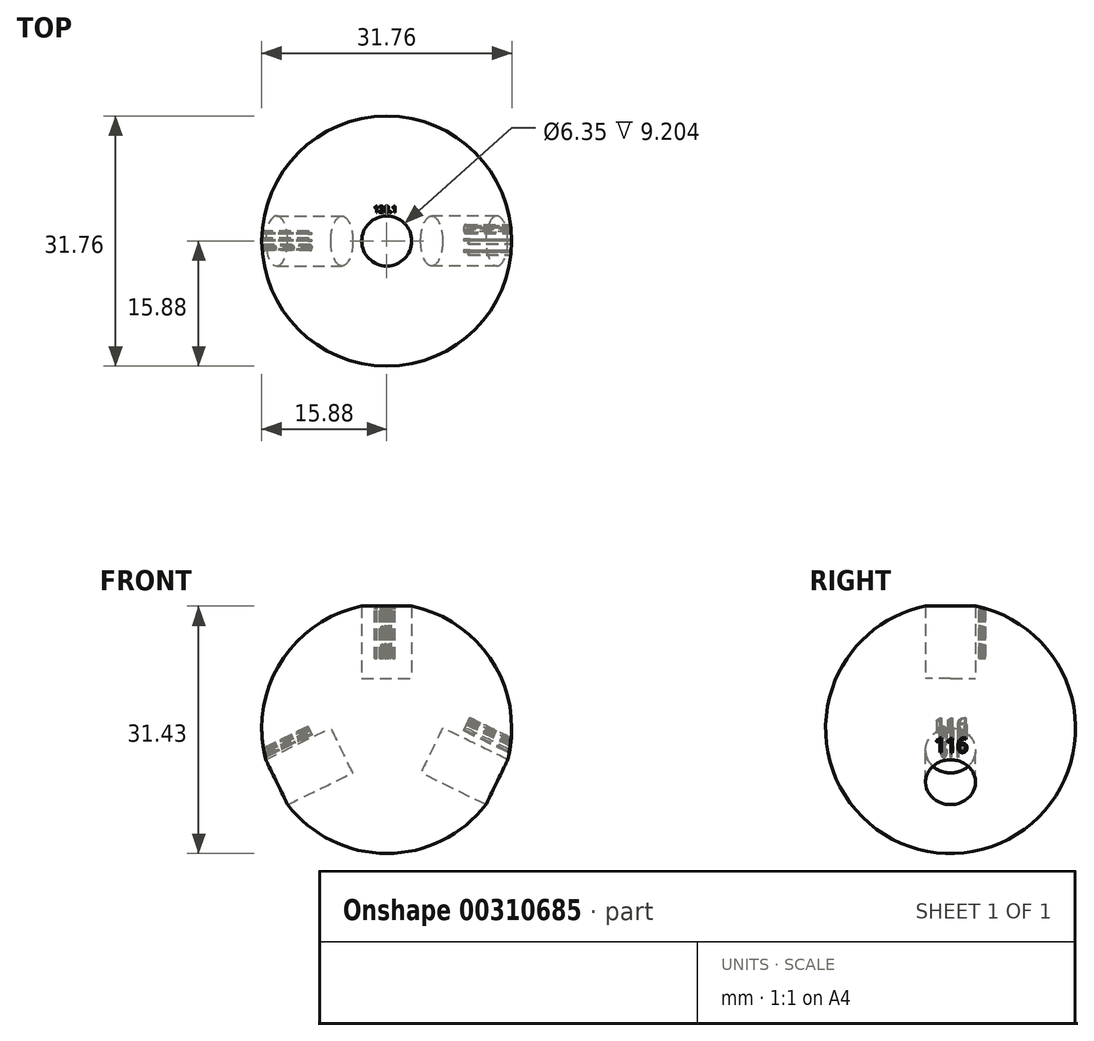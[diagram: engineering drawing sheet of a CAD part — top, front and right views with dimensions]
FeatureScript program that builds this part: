
annotation { "Feature Type Name" : "Feature", "Feature Type Description" : "" }
export const myFeature = defineFeature(function(context is Context, id is Id, definition is map)
    precondition{}
    {
        {
            var Q0;
            Q0=qCreatedBy(makeId("Front.planeOp"),FACE);
            var sketch = newSketch(context, id + "F0", { "sketchPlane" : qUnion([Q0])});
            skArc(sketch, "E0", {"start": v(-15.88, 0) * mm, "mid": v(0, -15.88) * mm, "end": v(15.88, 0) * mm});
            skLineSegment(sketch, "E1", {"start": v(-15.88, 0) * mm, "end": v(15.88, 0) * mm});
            skSolve(sketch);
        }
        {
            var Q0;
            Q0=qCreatedBy(makeId("Right.planeOp"),FACE);
            var sketch = newSketch(context, id + "F1", { "sketchPlane" : qUnion([Q0])});
            skCircle(sketch, "E2", {"center": v(0, 0) * mm, "radius": 15.88 * mm});
            skSolve(sketch);
        }
        {
            var Q0;
            Q0 = qSketchRegion(id + "F0", true);
            var Q1;
            Q1=sQuery(id+"F1.wireOp",EDGE,"E2");
            revolve(context, id + "F2", {"entities" : qUnion([Q0]), "axis" : qUnion([Q1]), "revolveType" : RevolveType.FULL});
        }
        {
            var Q0;
            Q0=qCreatedBy(makeId("Top.planeOp"),FACE);
            cPlane(context, id + "F3", {"entities" : qUnion([Q0]), "cplaneType" : CPlaneType.OFFSET, "offset" : 6.35 * mm, "width" : 152.4 * mm, "height" : 152.4 * mm});
        }
        {
            var Q0;
            Q0=qCreatedBy(id+"F3.planeOp",FACE);
            var sketch = newSketch(context, id + "F4", { "sketchPlane" : qUnion([Q0])});
            skCircle(sketch, "E3", {"center": v(0, 0) * mm, "radius": 3.18 * mm});
            skSolve(sketch);
        }
        {
            var Q0;
            Q0 = qSketchRegion(id + "F4", true);
            extrude(context, id + "F5", {"entities" : qUnion([Q0]), "depth" : 25.4 * mm});
        }
        {
            var Q0;
            Q0=makeQuery(id+"F5.opExtrude","CAP_FACE",FACE,{"disambiguationData":[OSD([sQuery(id+"F4.wireOp",EDGE,"E3")])],"isStart":false});
            cPlane(context, id + "F6", {"entities" : qUnion([Q0]), "cplaneType" : CPlaneType.OFFSET, "offset" : 12.7 * mm, "oppositeDirection" : true, "width" : 152.4 * mm, "height" : 152.4 * mm});
        }
        {
            var Q0;
            Q0=qCreatedBy(id+"F6.planeOp",FACE);
            var sketch = newSketch(context, id + "F7", { "sketchPlane" : qUnion([Q0])});
            skText(sketch, "E4", { "text": "128.1\n", "fontName": "OpenSans-Regular.ttf"});
            const initialGuessF7  = {"E4": [-0.00164, 0.00361, 1, 0, 0.00083]};
            skSetInitialGuess(sketch, initialGuessF7);
            skSolve(sketch);
        }
        {
            var Q0;
            Q0 = qSketchRegion(id + "F7", true);
            extrude(context, id + "F8", {"entities" : qUnion([Q0]), "operationType" : NewBodyOperationType.REMOVE, "oppositeDirection" : true, "depth" : 10.16 * mm});
        }
        {
            var Q0;
            Q0=qCreatedBy(makeId("Right.planeOp"),FACE);
            var sketch = newSketch(context, id + "F9", { "sketchPlane" : qUnion([Q0])});
            skLineSegment(sketch, "E5", {"start": v(66.37, 0) * mm, "end": v(-36.87, 0) * mm, "construction": true});
            skSolve(sketch);
        }
        {
            var Q0;
            Q0=makeQuery(id+"F5.opExtrude","SWEPT_BODY",BODY,{"disambiguationData":[OSD([sQuery(id+"F4.wireOp",EDGE,"E3")])]});
            var Q1;
            Q1=sQuery(id+"F9.wireOp",EDGE,"E5");
            transform(context, id + "F10", {"entities" : qUnion([Q0]), "transformType" : TransformType.ROTATION, "transformAxis" : qUnion([Q1]), "angle" : 116 * degree, "makeCopy" : true});
        }
        {
            var Q0;
            Q0=makeQuery(id+"F10.opPattern","COPY",FACE,{"derivedFrom":makeQuery(id+"F5.opExtrude","CAP_FACE",FACE,{"disambiguationData":[OSD([sQuery(id+"F4.wireOp",EDGE,"E3")])],"isStart":false}),"instanceName":"1"});
            cPlane(context, id + "F11", {"entities" : qUnion([Q0]), "cplaneType" : CPlaneType.OFFSET, "offset" : 12.7 * mm, "oppositeDirection" : true, "width" : 152.4 * mm, "height" : 152.4 * mm});
        }
        {
            var Q0;
            Q0=qCreatedBy(id+"F11.planeOp",FACE);
            var sketch = newSketch(context, id + "F12", { "sketchPlane" : qUnion([Q0])});
            skText(sketch, "E6", { "text": "116", "fontName": "OpenSans-Regular.ttf"});
            const initialGuessF12  = {"E6": [-0.00144, 0.00347, 1, 0, 0.00115]};
            skSetInitialGuess(sketch, initialGuessF12);
            skSolve(sketch);
        }
        {
            var Q0;
            Q0 = qSketchRegion(id + "F12", true);
            extrude(context, id + "F13", {"entities" : qUnion([Q0]), "operationType" : NewBodyOperationType.REMOVE, "oppositeDirection" : true, "depth" : 10.16 * mm});
        }
        {
            var Q0;
            Q0=qCreatedBy(makeId("Right.planeOp"),FACE);
            var sketch = newSketch(context, id + "F14", { "sketchPlane" : qUnion([Q0])});
            skLineSegment(sketch, "E7", {"start": v(59, 0) * mm, "end": v(-23.6, 0) * mm, "construction": true});
            skSolve(sketch);
        }
        {
            var Q0;
            Q0=makeQuery(id+"F5.opExtrude","SWEPT_BODY",BODY,{"disambiguationData":[OSD([sQuery(id+"F4.wireOp",EDGE,"E3")])]});
            var Q1;
            Q1=sQuery(id+"F14.wireOp",EDGE,"E7");
            transform(context, id + "F15", {"entities" : qUnion([Q0]), "transformType" : TransformType.ROTATION, "transformAxis" : qUnion([Q1]), "angle" : 116 * degree, "oppositeDirection" : true, "makeCopy" : true});
        }
        {
            var Q0;
            Q0=makeQuery(id+"F15.opPattern","COPY",FACE,{"derivedFrom":makeQuery(id+"F5.opExtrude","CAP_FACE",FACE,{"disambiguationData":[OSD([sQuery(id+"F4.wireOp",EDGE,"E3")])],"isStart":false}),"instanceName":"1"});
            cPlane(context, id + "F16", {"entities" : qUnion([Q0]), "cplaneType" : CPlaneType.OFFSET, "offset" : 12.7 * mm, "oppositeDirection" : true, "width" : 152.4 * mm, "height" : 152.4 * mm});
        }
        {
            var Q0;
            Q0=qCreatedBy(id+"F16.planeOp",FACE);
            var sketch = newSketch(context, id + "F17", { "sketchPlane" : qUnion([Q0])});
            skText(sketch, "E8", { "text": "116", "fontName": "OpenSans-Regular.ttf"});
            const initialGuessF17  = {"E8": [-0.00204, 0.00406, 1, 0, 0.00178]};
            skSetInitialGuess(sketch, initialGuessF17);
            skSolve(sketch);
        }
        {
            var Q0;
            Q0 = qSketchRegion(id + "F17", true);
            extrude(context, id + "F18", {"entities" : qUnion([Q0]), "operationType" : NewBodyOperationType.REMOVE, "oppositeDirection" : true, "depth" : 10.16 * mm});
        }
        {
            var Q0;
            Q0=makeQuery(id+"F5.opExtrude","SWEPT_BODY",BODY,{"disambiguationData":[OSD([sQuery(id+"F4.wireOp",EDGE,"E3")])]});
            var Q1;
            Q1=makeQuery(id+"F15.opPattern","COPY",BODY,{"derivedFrom":makeQuery(id+"F5.opExtrude","SWEPT_BODY",BODY,{"disambiguationData":[OSD([sQuery(id+"F4.wireOp",EDGE,"E3")])]}),"instanceName":"1"});
            var Q2;
            Q2=makeQuery(id+"F10.opPattern","COPY",BODY,{"derivedFrom":makeQuery(id+"F5.opExtrude","SWEPT_BODY",BODY,{"disambiguationData":[OSD([sQuery(id+"F4.wireOp",EDGE,"E3")])]}),"instanceName":"1"});
            var Q3;
            Q3=makeQuery(id+"F2.opRevolve","SWEPT_BODY",BODY,{"disambiguationData":[OSD([sQuery(id+"F0.wireOp",EDGE,"E0"),sQuery(id+"F0.wireOp",EDGE,"E1")])]});
            booleanBodies(context, id + "F19", {"operationType" : BooleanOperationType.SUBTRACTION, "tools" : qUnion([Q0, Q1, Q2]), "targets" : qUnion([Q3])});
        }
    });
